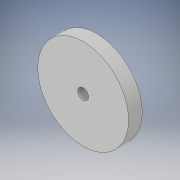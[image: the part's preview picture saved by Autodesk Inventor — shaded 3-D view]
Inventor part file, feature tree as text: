
AUTODESK INVENTOR PART (.ipt)
format: ipt  version: 2018 (Build 220112000, 112)  size: 95,744 bytes
history: native  units: in
note: dims shown in document units (in); Inventor stores cm internally (conversion verified against a paired STEP export)
features: extrude x1, sketch x1
ambient origin geometry x8: Origin, YZ Plane, XZ Plane, XY Plane, X Axis, Y Axis, Z Axis, Center Point
bodies: Solid1 (feature_tree)
feature tree (2):
  extrude  "Extrusion1"  Depth=0.75in
  sketch  "Sketch1"  dims[d0=0.6in d1=5.0in d2=0.75in d3=0.0in]
